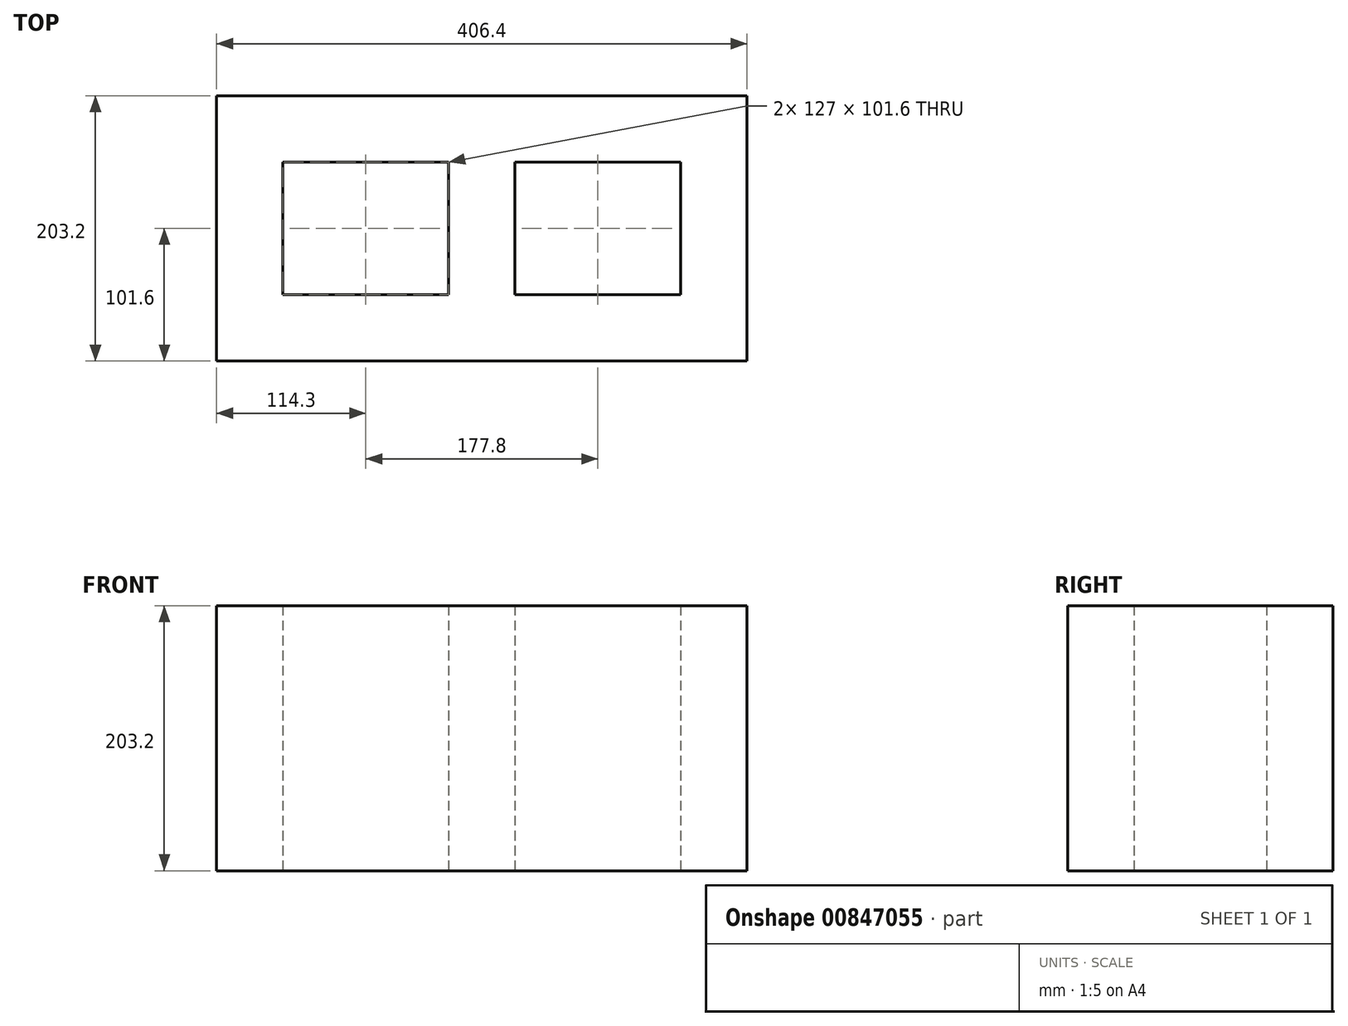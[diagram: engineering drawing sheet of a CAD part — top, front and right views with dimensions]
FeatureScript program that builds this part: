
annotation { "Feature Type Name" : "Feature", "Feature Type Description" : "" }
export const myFeature = defineFeature(function(context is Context, id is Id, definition is map)
    precondition{}
    {
        {
            var Q0;
            Q0=qCreatedBy(makeId("Top.planeOp"),FACE);
            var sketch = newSketch(context, id + "F0", { "sketchPlane" : qUnion([Q0])});
            skLineSegment(sketch, "E0.bottom", {"start": v(0, 0) * mm, "end": v(406.4, 0) * mm});
            skLineSegment(sketch, "E0.top", {"start": v(0, 203.2) * mm, "end": v(406.4, 203.2) * mm});
            skLineSegment(sketch, "E0.left", {"start": v(0, 0) * mm, "end": v(0, 203.2) * mm});
            skLineSegment(sketch, "E0.right", {"start": v(406.4, 0) * mm, "end": v(406.4, 203.2) * mm});
            skLineSegment(sketch, "E1.0", {"start": v(50.8, 50.8) * mm, "end": v(50.8, 152.4) * mm});
            skLineSegment(sketch, "E2.0", {"start": v(355.6, 50.8) * mm, "end": v(355.6, 152.4) * mm});
            skLineSegment(sketch, "E3", {"start": v(228.6, 152.4) * mm, "end": v(228.6, 50.8) * mm});
            skLineSegment(sketch, "E4", {"start": v(177.8, 152.4) * mm, "end": v(177.8, 50.8) * mm});
            skLineSegment(sketch, "E5.trimOffspring", {"start": v(228.6, 152.4) * mm, "end": v(355.6, 152.4) * mm});
            skLineSegment(sketch, "E6.trimOffspring", {"start": v(228.6, 50.8) * mm, "end": v(355.6, 50.8) * mm});
            skLineSegment(sketch, "E7", {"start": v(50.8, 152.4) * mm, "end": v(177.8, 152.4) * mm});
            skLineSegment(sketch, "E8", {"start": v(177.8, 50.8) * mm, "end": v(50.8, 50.8) * mm});
            skSolve(sketch);
        }
        {
            var Q0;
            Q0 = qSketchRegion(id + "F0", true);
            extrude(context, id + "F1", {"entities" : qUnion([Q0]), "depth" : 203.2 * mm, "offsetDistance" : 25.4 * mm});
        }
    });
